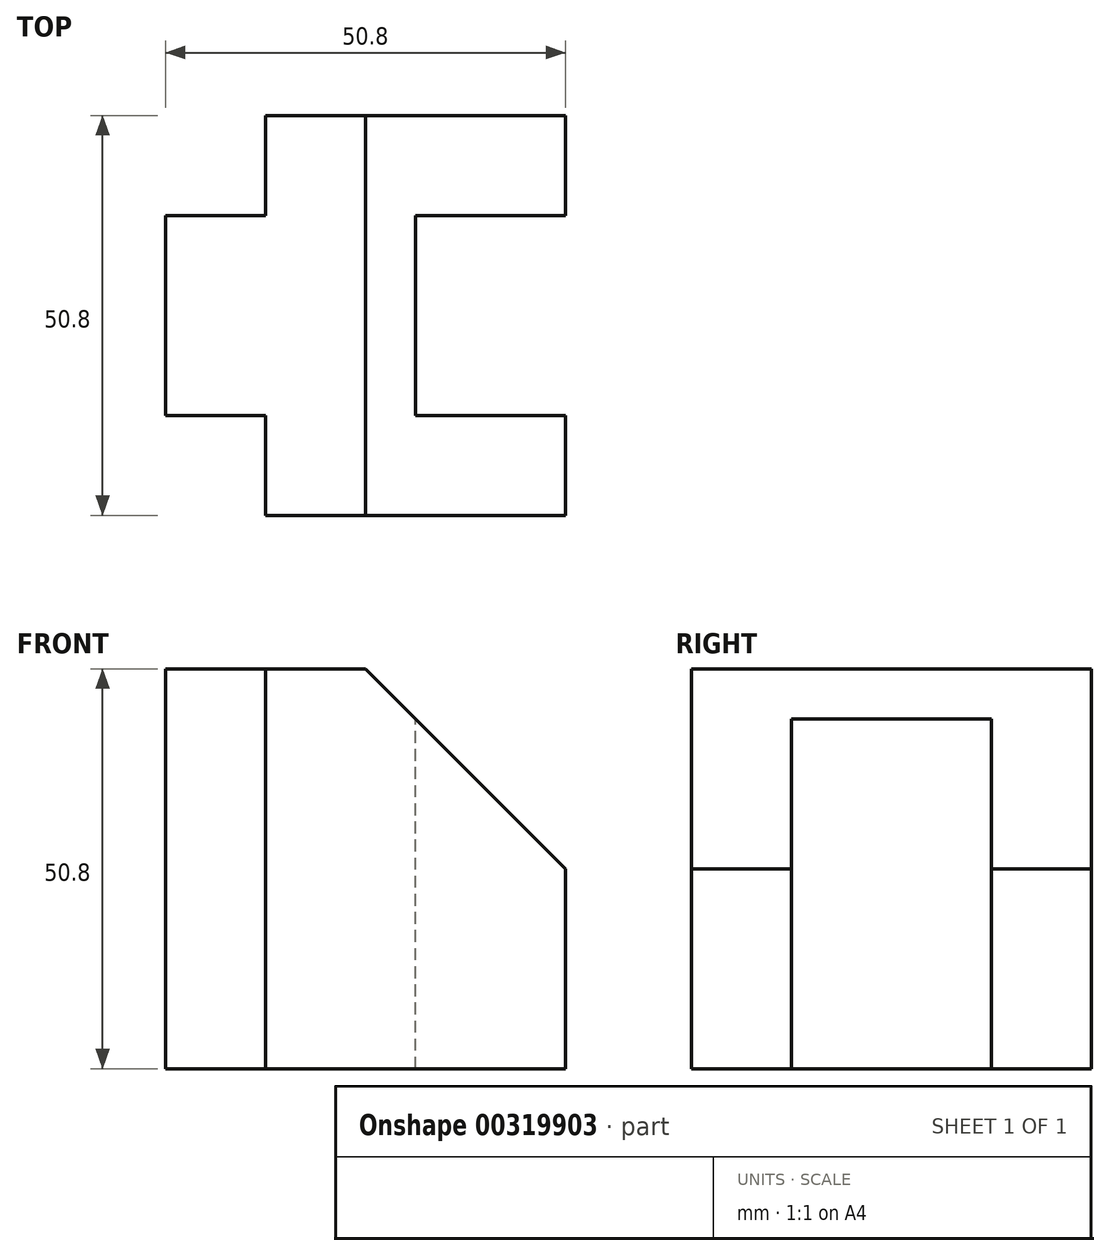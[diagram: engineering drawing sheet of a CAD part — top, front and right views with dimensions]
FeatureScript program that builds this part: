
annotation { "Feature Type Name" : "Feature", "Feature Type Description" : "" }
export const myFeature = defineFeature(function(context is Context, id is Id, definition is map)
    precondition{}
    {
        {
            var Q0;
            Q0=qCreatedBy(makeId("Front.planeOp"),FACE);
            var sketch = newSketch(context, id + "F0", { "sketchPlane" : qUnion([Q0])});
            skLineSegment(sketch, "E0", {"start": v(0, 0) * mm, "end": v(0, 50.8) * mm});
            skLineSegment(sketch, "E1", {"start": v(0, 50.8) * mm, "end": v(25.4, 50.8) * mm});
            skLineSegment(sketch, "E2", {"start": v(0, 50.8) * mm, "end": v(12.7, 50.8) * mm});
            skLineSegment(sketch, "E3", {"start": v(12.7, 50.8) * mm, "end": v(12.7, 0) * mm});
            skLineSegment(sketch, "E4", {"start": v(0, 0) * mm, "end": v(50.8, 0) * mm});
            skLineSegment(sketch, "E5", {"start": v(50.8, 0) * mm, "end": v(50.8, 25.4) * mm});
            skLineSegment(sketch, "E6", {"start": v(50.8, 25.4) * mm, "end": v(25.4, 50.8) * mm});
            skSolve(sketch);
        }
        {
            var Q0;
            Q0 = qSketchRegion(id + "F0", true);
            extrude(context, id + "F1", {"entities" : qUnion([Q0]), "endBound" : BoundingType.SYMMETRIC, "depth" : 50.8 * mm});
        }
        {
            var Q0;
            Q0=makeQuery(id+"F1.opExtrude","SWEPT_FACE",FACE,{"disambiguationData":[OSD([sQuery(id+"F0.wireOp",EDGE,"E1"),sQuery(id+"F0.wireOp",EDGE,"E2")])]});
            var sketch = newSketch(context, id + "F2", { "sketchPlane" : qUnion([Q0])});
            skLineSegment(sketch, "E7.bottom", {"start": v(0, 25.4) * mm, "end": v(12.7, 25.4) * mm});
            skLineSegment(sketch, "E7.top", {"start": v(0, 12.7) * mm, "end": v(12.7, 12.7) * mm});
            skLineSegment(sketch, "E7.left", {"start": v(0, 25.4) * mm, "end": v(0, 12.7) * mm});
            skLineSegment(sketch, "E7.right", {"start": v(12.7, 25.4) * mm, "end": v(12.7, 12.7) * mm});
            skLineSegment(sketch, "E8.bottom", {"start": v(0, -25.4) * mm, "end": v(12.7, -25.4) * mm});
            skLineSegment(sketch, "E8.top", {"start": v(0, -12.7) * mm, "end": v(12.7, -12.7) * mm});
            skLineSegment(sketch, "E8.left", {"start": v(0, -25.4) * mm, "end": v(0, -12.7) * mm});
            skLineSegment(sketch, "E8.right", {"start": v(12.7, -25.4) * mm, "end": v(12.7, -12.7) * mm});
            skSolve(sketch);
        }
        {
            var Q0;
            Q0 = qSketchRegion(id + "F2", true);
            extrude(context, id + "F3", {"entities" : qUnion([Q0]), "operationType" : NewBodyOperationType.REMOVE, "endBound" : BoundingType.THROUGH_ALL, "oppositeDirection" : true, "depth" : 25.4 * mm});
        }
        {
            var Q0;
            Q0=qCreatedBy(makeId("Front.planeOp"),FACE);
            var sketch = newSketch(context, id + "F4", { "sketchPlane" : qUnion([Q0])});
            skLineSegment(sketch, "E9", {"start": v(50.8, 0) * mm, "end": v(31.75, 0) * mm});
            skLineSegment(sketch, "E10", {"start": v(31.75, 0) * mm, "end": v(31.75, 44.45) * mm});
            skLineSegment(sketch, "E11", {"start": v(31.75, 44.45) * mm, "end": v(50.8, 25.4) * mm});
            skLineSegment(sketch, "E12", {"start": v(50.8, 25.4) * mm, "end": v(50.8, 0) * mm});
            skSolve(sketch);
        }
        {
            var Q0;
            Q0 = qSketchRegion(id + "F4", true);
            extrude(context, id + "F5", {"entities" : qUnion([Q0]), "operationType" : NewBodyOperationType.REMOVE, "endBound" : BoundingType.SYMMETRIC, "oppositeDirection" : true, "depth" : 25.4 * mm});
        }
    });
